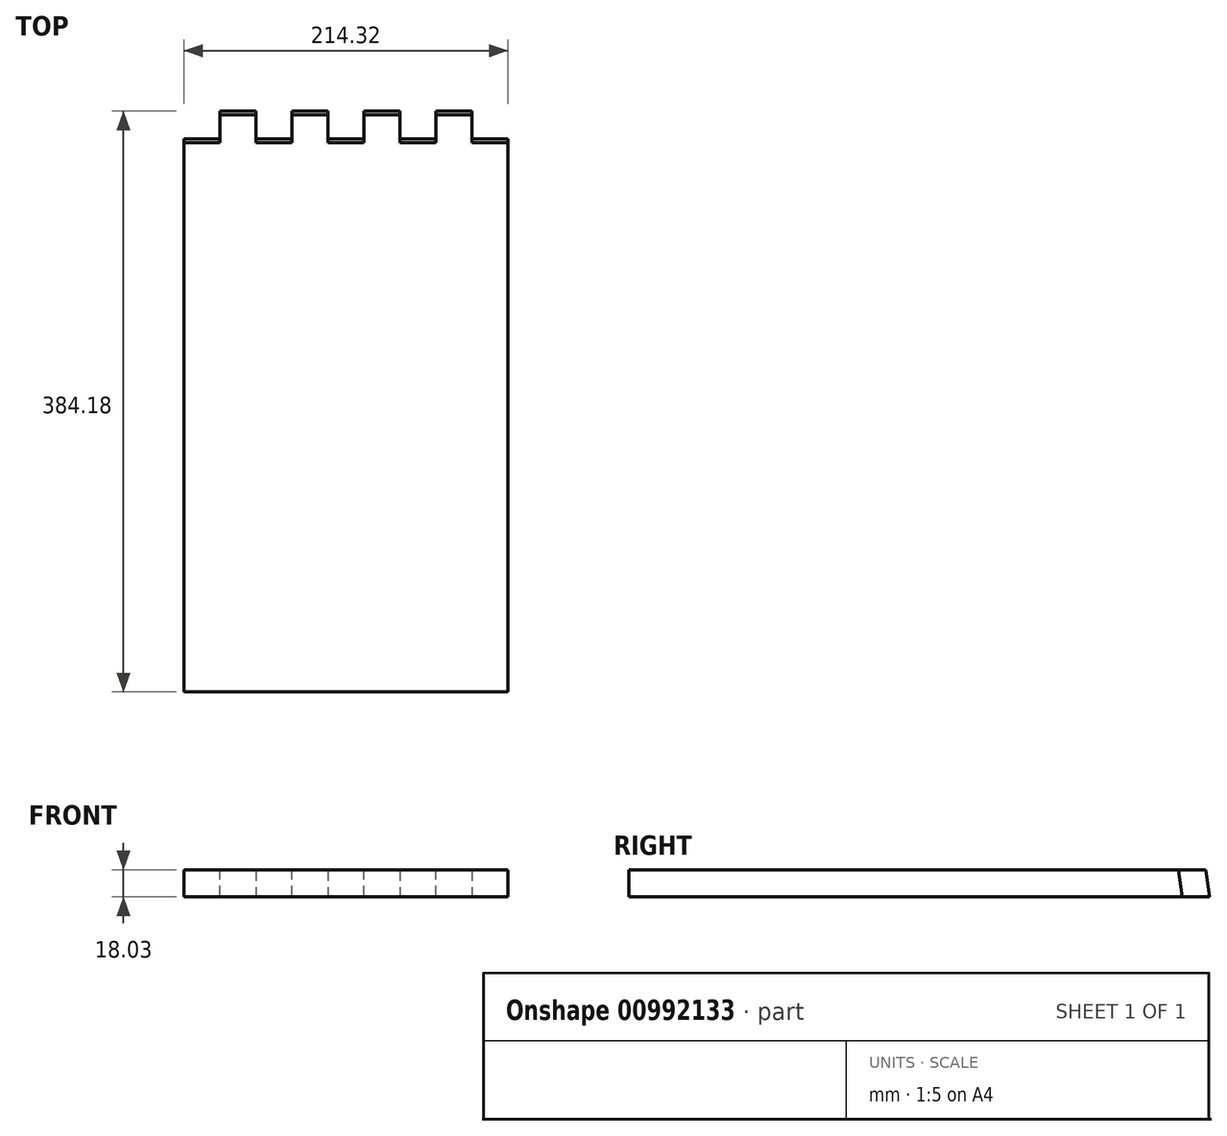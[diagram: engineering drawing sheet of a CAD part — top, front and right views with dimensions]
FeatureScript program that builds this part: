
annotation { "Feature Type Name" : "Feature", "Feature Type Description" : "" }
export const myFeature = defineFeature(function(context is Context, id is Id, definition is map)
    precondition{}
    {
        {
            var Q0;
            Q0=qCreatedBy(makeId("Top.planeOp"),FACE);
            var sketch = newSketch(context, id + "F0", { "sketchPlane" : qUnion([Q0])});
            skLineSegment(sketch, "E0", {"start": v(-107.16, 192.09) * mm, "end": v(-107.16, -192.09) * mm});
            skLineSegment(sketch, "E1", {"start": v(-107.16, -192.09) * mm, "end": v(107.16, -192.09) * mm});
            skLineSegment(sketch, "E2", {"start": v(107.16, -192.09) * mm, "end": v(107.16, 192.09) * mm});
            skLineSegment(sketch, "E3", {"start": v(107.16, 192.09) * mm, "end": v(-107.16, 192.09) * mm});
            skSolve(sketch);
        }
        {
            var Q0;
            Q0 = qSketchRegion(id + "F0", true);
            extrude(context, id + "F1", {"entities" : qUnion([Q0]), "depth" : 18.03 * mm, "offsetDistance" : 25.4 * mm});
        }
        {
            var Q0;
            Q0=makeQuery(id+"F1.opExtrude","SWEPT_FACE",FACE,{"disambiguationData":[OSD([sQuery(id+"F0.wireOp",EDGE,"E0")])]});
            var sketch = newSketch(context, id + "F2", { "sketchPlane" : qUnion([Q0])});
            skLineSegment(sketch, "E4", {"start": v(-192.09, 0) * mm, "end": v(-189.55, 18.03) * mm});
            skLineSegment(sketch, "E5", {"start": v(-189.55, 18.03) * mm, "end": v(-204.79, 18.03) * mm});
            skLineSegment(sketch, "E6", {"start": v(-204.79, 18.03) * mm, "end": v(-204.79, 0) * mm});
            skLineSegment(sketch, "E7", {"start": v(-204.79, 0) * mm, "end": v(-192.09, 0) * mm});
            skSolve(sketch);
        }
        {
            var Q0;
            Q0 = qSketchRegion(id + "F2", true);
            var Q1;
            Q1=makeQuery(id+"F1.opExtrude","SWEPT_FACE",FACE,{"disambiguationData":[OSD([sQuery(id+"F0.wireOp",EDGE,"E2")])]});
            extrude(context, id + "F3", {"entities" : qUnion([Q0]), "operationType" : NewBodyOperationType.REMOVE, "endBound" : BoundingType.UP_TO_SURFACE, "oppositeDirection" : true, "depth" : 25.4 * mm, "endBoundEntityFace" : qUnion([Q1]), "offsetDistance" : 25.4 * mm});
        }
        {
            var Q0;
            Q0=makeQuery(id+"F3.boolean.opBoolean","COPY",FACE,{"derivedFrom":makeQuery(id+"F3.opExtrude","SWEPT_FACE",FACE,{"disambiguationData":[OSD([sQuery(id+"F2.wireOp",EDGE,"E4")])]})});
            cPlane(context, id + "F4", {"entities" : qUnion([Q0]), "cplaneType" : CPlaneType.OFFSET, "offset" : 0 * mm, "width" : 152.4 * mm, "height" : 152.4 * mm});
        }
        {
            var Q0;
            Q0=qCreatedBy(id+"F4.planeOp",FACE);
            var sketch = newSketch(context, id + "F5", { "sketchPlane" : qUnion([Q0])});
            skLineSegment(sketch, "E8", {"start": v(-107.16, -1.33) * mm, "end": v(-83.34, -1.33) * mm});
            skLineSegment(sketch, "E9", {"start": v(-83.34, -1.33) * mm, "end": v(-83.34, -26.73) * mm});
            skLineSegment(sketch, "E10", {"start": v(-83.34, -26.73) * mm, "end": v(-59.53, -26.73) * mm});
            skLineSegment(sketch, "E11", {"start": v(-59.53, -26.73) * mm, "end": v(-59.53, -1.33) * mm});
            skLineSegment(sketch, "E12", {"start": v(-59.53, -1.33) * mm, "end": v(-35.72, -1.33) * mm});
            skLineSegment(sketch, "E13", {"start": v(-35.72, -1.33) * mm, "end": v(-35.72, -26.73) * mm});
            skLineSegment(sketch, "E14", {"start": v(-35.72, -26.73) * mm, "end": v(-11.9, -26.73) * mm});
            skLineSegment(sketch, "E15", {"start": v(-11.9, -26.73) * mm, "end": v(-11.9, -1.33) * mm});
            skLineSegment(sketch, "E16", {"start": v(-11.9, -1.33) * mm, "end": v(11.9, -1.33) * mm});
            skLineSegment(sketch, "E17", {"start": v(11.9, -1.33) * mm, "end": v(11.9, -26.73) * mm});
            skLineSegment(sketch, "E18", {"start": v(11.9, -26.73) * mm, "end": v(35.72, -26.73) * mm});
            skLineSegment(sketch, "E19", {"start": v(35.72, -26.73) * mm, "end": v(35.72, -1.33) * mm});
            skLineSegment(sketch, "E20", {"start": v(35.72, -1.33) * mm, "end": v(59.53, -1.33) * mm});
            skLineSegment(sketch, "E21", {"start": v(59.53, -1.33) * mm, "end": v(59.53, -26.73) * mm});
            skLineSegment(sketch, "E22", {"start": v(59.53, -26.73) * mm, "end": v(83.34, -26.73) * mm});
            skLineSegment(sketch, "E23", {"start": v(107.16, -33.08) * mm, "end": v(-107.16, -33.08) * mm});
            skLineSegment(sketch, "E24", {"start": v(-107.16, -1.33) * mm, "end": v(-107.16, -26.73) * mm});
            skLineSegment(sketch, "E25", {"start": v(-107.16, -26.73) * mm, "end": v(-107.16, -33.08) * mm});
            skLineSegment(sketch, "E26", {"start": v(83.34, -26.73) * mm, "end": v(83.34, -1.33) * mm});
            skLineSegment(sketch, "E27", {"start": v(83.34, -1.33) * mm, "end": v(107.16, -1.33) * mm});
            skLineSegment(sketch, "E28", {"start": v(107.16, -1.33) * mm, "end": v(107.16, -26.73) * mm});
            skLineSegment(sketch, "E29", {"start": v(107.16, -26.73) * mm, "end": v(107.16, -33.08) * mm});
            skSolve(sketch);
        }
        {
            var Q0;
            Q0 = qSketchRegion(id + "F5", true);
            extrude(context, id + "F6", {"entities" : qUnion([Q0]), "operationType" : NewBodyOperationType.REMOVE, "oppositeDirection" : true, "depth" : 18.03 * mm, "offsetDistance" : 25.4 * mm});
        }
    });
